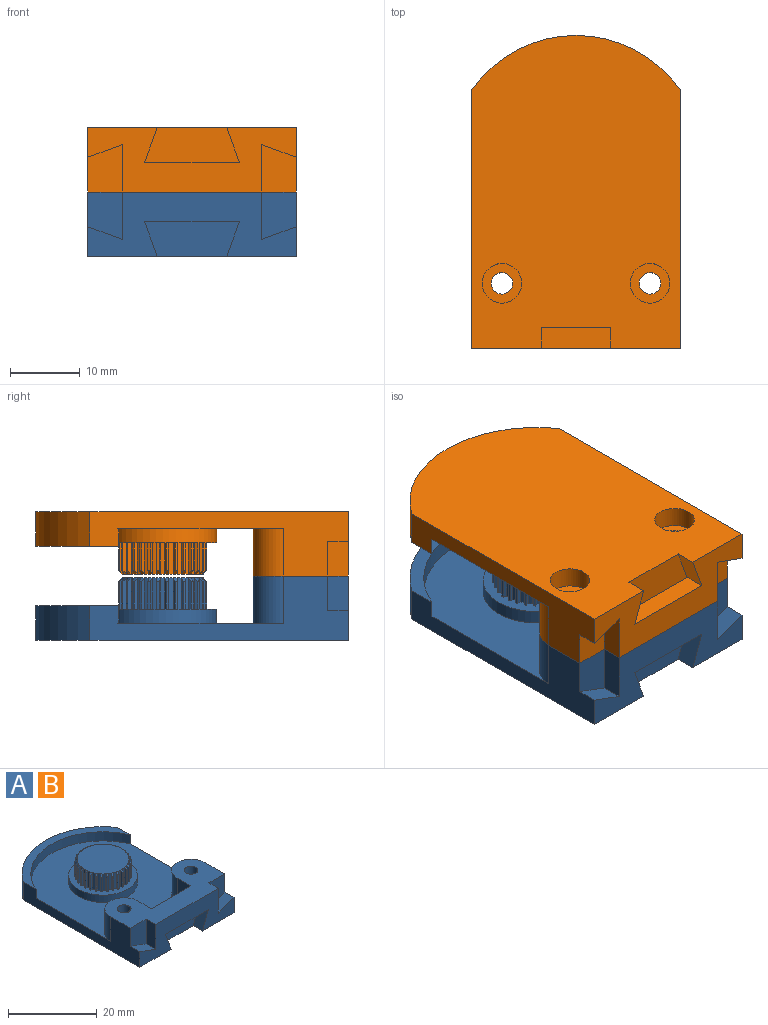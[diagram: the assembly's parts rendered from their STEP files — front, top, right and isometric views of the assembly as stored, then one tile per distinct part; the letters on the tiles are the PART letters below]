
ASSEMBLY  parts=2 mates=1
PART A: 183 faces, bbox 30x45x9.3 mm
  f0: plane 45x30mm, normal (0,0,-1), area 1198.9mm2, adj f3,f4,f5,f162,f163,f165,f176,f178
  f1: plane 12.6x6.77mm, normal (0,1,0), area 85.3mm2, adj f2,f154,f173,f174
  f2: plane 30x13.7mm, normal (0,0,1), area 240mm2, adj f1,f3,f4,f5,f152,f153,f167,f168
  f3: plane 37.17x9.27mm, normal (1,0,0), area 151.5mm2, adj f0,f2,f5,f154,f170,f171,f172,f180
  f4: plane 37.17x9.27mm, normal (-1,0,0), area 151.5mm2, adj f0,f2,f5,f154,f166,f168,f175,f180
  f5: plane 30x9.27mm, normal (0,-1,0), area 159.9mm2, adj f0,f2,f3,f4,f162,f163,f164,f166
  f6: cone r=5.85mm half-angle=45deg, axis (0,0,-1), area 0.3mm2, adj f7,f10,f157,f159
  f7: cylinder r=6.35mm len=4mm, axis (0,0,-1), area 1.3mm2, adj f6,f10,f156,f159
  f8: plane 4.51x0.45mm, normal (0.53,-0.85,0), area 2.2mm2, adj f9,f11,f12,f156
  f9: cylinder r=5.85mm len=4.5mm, axis (0,0,-1), area 2.9mm2, adj f8,f10,f156,f157
  f10: plane 4.51x0.52mm, normal (0.14,0.99,0), area 2.2mm2, adj f6,f7,f9,f156
  f11: cone r=5.85mm half-angle=45deg, axis (0,0,-1), area 0.3mm2, adj f8,f12,f15,f157
  f12: cylinder r=6.35mm len=4mm, axis (0,0,-1), area 1.3mm2, adj f8,f11,f15,f156
  f13: plane 4.51x0.38mm, normal (0.69,-0.72,0), area 2.2mm2, adj f14,f16,f17,f156
  f14: cylinder r=5.85mm len=4.5mm, axis (0,0,-1), area 2.9mm2, adj f13,f15,f156,f157
  f15: plane 4.51x0.53mm, normal (-0.07,1,0), area 2.2mm2, adj f11,f12,f14,f156
  f16: cone r=5.85mm half-angle=45deg, axis (0,0,-1), area 0.3mm2, adj f13,f17,f20,f157
  f17: cylinder r=6.35mm len=4mm, axis (0,0,-1), area 1.3mm2, adj f13,f16,f20,f156
  f18: plane 4.51x0.44mm, normal (0.83,-0.56,0), area 2.2mm2, adj f19,f21,f22,f156
  f19: cylinder r=5.85mm len=4.5mm, axis (0,0,-1), area 2.9mm2, adj f18,f20,f156,f157
  f20: plane 4.51x0.51mm, normal (-0.28,0.96,0), area 2.2mm2, adj f16,f17,f19,f156
  f21: cone r=5.85mm half-angle=45deg, axis (0,0,-1), area 0.3mm2, adj f18,f22,f25,f157
  f22: cylinder r=6.35mm len=4mm, axis (0,0,-1), area 1.3mm2, adj f18,f21,f25,f156
  f23: plane 4.51x0.49mm, normal (0.93,-0.37,0), area 2.2mm2, adj f24,f26,f27,f156
  f24: cylinder r=5.85mm len=4.5mm, axis (0,0,-1), area 2.9mm2, adj f23,f25,f156,f157
  f25: plane 4.51x0.47mm, normal (-0.47,0.88,0), area 2.2mm2, adj f21,f22,f24,f156
  f26: cone r=5.85mm half-angle=45deg, axis (0,0,-1), area 0.3mm2, adj f23,f27,f30,f157
  f27: cylinder r=6.35mm len=4mm, axis (0,0,-1), area 1.3mm2, adj f23,f26,f30,f156
  f28: plane 4.51x0.52mm, normal (0.98,-0.17,0), area 2.2mm2, adj f29,f31,f32,f156
  f29: cylinder r=5.85mm len=4.5mm, axis (0,0,-1), area 2.9mm2, adj f28,f30,f156,f157
  f30: plane 4.51x0.4mm, normal (-0.64,0.77,0), area 2.2mm2, adj f26,f27,f29,f156
  f31: cone r=5.85mm half-angle=45deg, axis (0,0,-1), area 0.3mm2, adj f28,f32,f35,f157
  f32: cylinder r=6.35mm len=4mm, axis (0,0,-1), area 1.3mm2, adj f28,f31,f35,f156
  f33: plane 4.51x0.53mm, normal (1,0.03,0), area 2.2mm2, adj f34,f36,f37,f156
  f34: cylinder r=5.85mm len=4.5mm, axis (0,0,-1), area 2.9mm2, adj f33,f35,f156,f157
  f35: plane 4.51x0.42mm, normal (-0.79,0.62,0), area 2.2mm2, adj f31,f32,f34,f156
  f36: cone r=5.85mm half-angle=45deg, axis (0,0,-1), area 0.3mm2, adj f33,f37,f40,f157
  f37: cylinder r=6.35mm len=4mm, axis (0,0,-1), area 1.3mm2, adj f33,f36,f40,f156
  f38: plane 4.51x0.51mm, normal (0.97,0.24,0), area 2.2mm2, adj f39,f41,f42,f156
  f39: cylinder r=5.85mm len=4.5mm, axis (0,0,-1), area 2.9mm2, adj f38,f40,f156,f157
  f40: plane 4.51x0.47mm, normal (-0.9,0.44,0), area 2.2mm2, adj f36,f37,f39,f156
  f41: cone r=5.85mm half-angle=45deg, axis (0,0,-1), area 0.3mm2, adj f38,f42,f45,f157
  f42: cylinder r=6.35mm len=4mm, axis (0,0,-1), area 1.3mm2, adj f38,f41,f45,f156
  f43: plane 4.51x0.47mm, normal (0.9,0.44,0), area 2.2mm2, adj f44,f46,f47,f156
  f44: cylinder r=5.85mm len=4.5mm, axis (0,0,-1), area 2.9mm2, adj f43,f45,f156,f157
  f45: plane 4.51x0.51mm, normal (-0.97,0.24,0), area 2.2mm2, adj f41,f42,f44,f156
  f46: cone r=5.85mm half-angle=45deg, axis (0,0,-1), area 0.3mm2, adj f43,f47,f50,f157
  f47: cylinder r=6.35mm len=4mm, axis (0,0,-1), area 1.3mm2, adj f43,f46,f50,f156
  f48: plane 4.51x0.42mm, normal (0.79,0.62,0), area 2.2mm2, adj f49,f51,f52,f156
  f49: cylinder r=5.85mm len=4.5mm, axis (0,0,-1), area 2.9mm2, adj f48,f50,f156,f157
  f50: plane 4.51x0.53mm, normal (-1,0.03,0), area 2.2mm2, adj f46,f47,f49,f156
  f51: cone r=5.85mm half-angle=45deg, axis (0,0,-1), area 0.3mm2, adj f48,f52,f55,f157
  f52: cylinder r=6.35mm len=4mm, axis (0,0,-1), area 1.3mm2, adj f48,f51,f55,f156
  f53: plane 4.51x0.4mm, normal (0.64,0.77,0), area 2.2mm2, adj f54,f56,f57,f156
  f54: cylinder r=5.85mm len=4.5mm, axis (0,0,-1), area 2.9mm2, adj f53,f55,f156,f157
  f55: plane 4.51x0.52mm, normal (-0.98,-0.17,0), area 2.2mm2, adj f51,f52,f54,f156
  f56: cone r=5.85mm half-angle=45deg, axis (0,0,-1), area 0.3mm2, adj f53,f57,f60,f157
  f57: cylinder r=6.35mm len=4mm, axis (0,0,-1), area 1.3mm2, adj f53,f56,f60,f156
  f58: plane 4.51x0.47mm, normal (0.47,0.88,0), area 2.2mm2, adj f59,f61,f62,f156
  f59: cylinder r=5.85mm len=4.5mm, axis (0,0,-1), area 2.9mm2, adj f58,f60,f156,f157
  f60: plane 4.51x0.49mm, normal (-0.93,-0.37,0), area 2.2mm2, adj f56,f57,f59,f156
  f61: cone r=5.85mm half-angle=45deg, axis (0,0,-1), area 0.3mm2, adj f58,f62,f65,f157
  f62: cylinder r=6.35mm len=4mm, axis (0,0,-1), area 1.3mm2, adj f58,f61,f65,f156
  f63: plane 4.51x0.51mm, normal (0.28,0.96,0), area 2.2mm2, adj f64,f66,f67,f156
  f64: cylinder r=5.85mm len=4.5mm, axis (0,0,-1), area 2.9mm2, adj f63,f65,f156,f157
  f65: plane 4.51x0.44mm, normal (-0.83,-0.56,0), area 2.2mm2, adj f61,f62,f64,f156
  f66: cone r=5.85mm half-angle=45deg, axis (0,0,-1), area 0.3mm2, adj f63,f67,f70,f157
  f67: cylinder r=6.35mm len=4mm, axis (0,0,-1), area 1.3mm2, adj f63,f66,f70,f156
  f68: plane 4.51x0.53mm, normal (0.07,1,0), area 2.2mm2, adj f69,f71,f72,f156
  f69: cylinder r=5.85mm len=4.5mm, axis (0,0,-1), area 2.9mm2, adj f68,f70,f156,f157
  f70: plane 4.51x0.38mm, normal (-0.69,-0.72,0), area 2.2mm2, adj f66,f67,f69,f156
  f71: cone r=5.85mm half-angle=45deg, axis (0,0,-1), area 0.3mm2, adj f68,f72,f75,f157
  f72: cylinder r=6.35mm len=4mm, axis (0,0,-1), area 1.3mm2, adj f68,f71,f75,f156
  f73: plane 4.51x0.52mm, normal (-0.14,0.99,0), area 2.2mm2, adj f74,f76,f77,f156
  f74: cylinder r=5.85mm len=4.5mm, axis (0,0,-1), area 2.9mm2, adj f73,f75,f156,f157
  f75: plane 4.51x0.45mm, normal (-0.53,-0.85,0), area 2.2mm2, adj f71,f72,f74,f156
  f76: cone r=5.85mm half-angle=45deg, axis (0,0,-1), area 0.3mm2, adj f73,f77,f80,f157
  f77: cylinder r=6.35mm len=4mm, axis (0,0,-1), area 1.3mm2, adj f73,f76,f80,f156
  f78: plane 4.51x0.5mm, normal (-0.34,0.94,0), area 2.2mm2, adj f79,f81,f82,f156
  f79: cylinder r=5.85mm len=4.5mm, axis (0,0,-1), area 2.9mm2, adj f78,f80,f156,f157
  f80: plane 4.51x0.5mm, normal (-0.34,-0.94,0), area 2.2mm2, adj f76,f77,f79,f156
  f81: cone r=5.85mm half-angle=45deg, axis (0,0,-1), area 0.3mm2, adj f78,f82,f85,f157
  f82: cylinder r=6.35mm len=4mm, axis (0,0,-1), area 1.3mm2, adj f78,f81,f85,f156
  f83: plane 4.51x0.45mm, normal (-0.53,0.85,0), area 2.2mm2, adj f84,f86,f87,f156
  f84: cylinder r=5.85mm len=4.5mm, axis (0,0,-1), area 2.9mm2, adj f83,f85,f156,f157
  f85: plane 4.51x0.52mm, normal (-0.14,-0.99,0), area 2.2mm2, adj f81,f82,f84,f156
  f86: cone r=5.85mm half-angle=45deg, axis (0,0,-1), area 0.3mm2, adj f83,f87,f90,f157
  f87: cylinder r=6.35mm len=4mm, axis (0,0,-1), area 1.3mm2, adj f83,f86,f90,f156
  f88: plane 4.51x0.38mm, normal (-0.69,0.72,0), area 2.2mm2, adj f89,f91,f92,f156
  f89: cylinder r=5.85mm len=4.5mm, axis (0,0,-1), area 2.9mm2, adj f88,f90,f156,f157
  f90: plane 4.51x0.53mm, normal (0.07,-1,0), area 2.2mm2, adj f86,f87,f89,f156
  f91: cone r=5.85mm half-angle=45deg, axis (0,0,-1), area 0.3mm2, adj f88,f92,f95,f157
  f92: cylinder r=6.35mm len=4mm, axis (0,0,-1), area 1.3mm2, adj f88,f91,f95,f156
  f93: plane 4.51x0.44mm, normal (-0.83,0.56,0), area 2.2mm2, adj f94,f96,f97,f156
  f94: cylinder r=5.85mm len=4.5mm, axis (0,0,-1), area 2.9mm2, adj f93,f95,f156,f157
  f95: plane 4.51x0.51mm, normal (0.28,-0.96,0), area 2.2mm2, adj f91,f92,f94,f156
  f96: cone r=5.85mm half-angle=45deg, axis (0,0,-1), area 0.3mm2, adj f93,f97,f100,f157
  f97: cylinder r=6.35mm len=4mm, axis (0,0,-1), area 1.3mm2, adj f93,f96,f100,f156
  f98: plane 4.51x0.49mm, normal (-0.93,0.37,0), area 2.2mm2, adj f99,f101,f102,f156
  f99: cylinder r=5.85mm len=4.5mm, axis (0,0,-1), area 2.9mm2, adj f98,f100,f156,f157
  f100: plane 4.51x0.47mm, normal (0.47,-0.88,0), area 2.2mm2, adj f96,f97,f99,f156
  f101: cone r=5.85mm half-angle=45deg, axis (0,0,-1), area 0.3mm2, adj f98,f102,f105,f157
  f102: cylinder r=6.35mm len=4mm, axis (0,0,-1), area 1.3mm2, adj f98,f101,f105,f156
  f103: plane 4.51x0.52mm, normal (-0.98,0.17,0), area 2.2mm2, adj f104,f106,f107,f156
  f104: cylinder r=5.85mm len=4.5mm, axis (0,0,-1), area 2.9mm2, adj f103,f105,f156,f157
  f105: plane 4.51x0.4mm, normal (0.64,-0.77,0), area 2.2mm2, adj f101,f102,f104,f156
  f106: cone r=5.85mm half-angle=45deg, axis (0,0,-1), area 0.3mm2, adj f103,f107,f110,f157
  f107: cylinder r=6.35mm len=4mm, axis (0,0,-1), area 1.3mm2, adj f103,f106,f110,f156
  f108: plane 4.51x0.53mm, normal (-1,-0.03,0), area 2.2mm2, adj f109,f111,f112,f156
  f109: cylinder r=5.85mm len=4.5mm, axis (0,0,-1), area 2.9mm2, adj f108,f110,f156,f157
  f110: plane 4.51x0.42mm, normal (0.79,-0.62,0), area 2.2mm2, adj f106,f107,f109,f156
  f111: cone r=5.85mm half-angle=45deg, axis (0,0,-1), area 0.3mm2, adj f108,f112,f115,f157
  f112: cylinder r=6.35mm len=4mm, axis (0,0,-1), area 1.3mm2, adj f108,f111,f115,f156
  f113: plane 4.51x0.51mm, normal (-0.97,-0.24,0), area 2.2mm2, adj f114,f116,f117,f156
  f114: cylinder r=5.85mm len=4.5mm, axis (0,0,-1), area 2.9mm2, adj f113,f115,f156,f157
  f115: plane 4.51x0.47mm, normal (0.9,-0.44,0), area 2.2mm2, adj f111,f112,f114,f156
  f116: cone r=5.85mm half-angle=45deg, axis (0,0,-1), area 0.3mm2, adj f113,f117,f120,f157
  f117: cylinder r=6.35mm len=4mm, axis (0,0,-1), area 1.3mm2, adj f113,f116,f120,f156
  f118: plane 4.51x0.47mm, normal (-0.9,-0.44,0), area 2.2mm2, adj f119,f121,f122,f156
  f119: cylinder r=5.85mm len=4.5mm, axis (0,0,-1), area 2.9mm2, adj f118,f120,f156,f157
  f120: plane 4.51x0.51mm, normal (0.97,-0.24,0), area 2.2mm2, adj f116,f117,f119,f156
  f121: cone r=5.85mm half-angle=45deg, axis (0,0,-1), area 0.3mm2, adj f118,f122,f125,f157
  f122: cylinder r=6.35mm len=4mm, axis (0,0,-1), area 1.3mm2, adj f118,f121,f125,f156
  f123: plane 4.51x0.42mm, normal (-0.79,-0.62,0), area 2.2mm2, adj f124,f126,f127,f156
  f124: cylinder r=5.85mm len=4.5mm, axis (0,0,-1), area 2.9mm2, adj f123,f125,f156,f157
  f125: plane 4.51x0.53mm, normal (1,-0.03,0), area 2.2mm2, adj f121,f122,f124,f156
  f126: cone r=5.85mm half-angle=45deg, axis (0,0,-1), area 0.3mm2, adj f123,f127,f130,f157
  f127: cylinder r=6.35mm len=4mm, axis (0,0,-1), area 1.3mm2, adj f123,f126,f130,f156
  f128: plane 4.51x0.4mm, normal (-0.64,-0.77,0), area 2.2mm2, adj f129,f131,f132,f156
  f129: cylinder r=5.85mm len=4.5mm, axis (0,0,-1), area 2.9mm2, adj f128,f130,f156,f157
  f130: plane 4.51x0.52mm, normal (0.98,0.17,0), area 2.2mm2, adj f126,f127,f129,f156
  f131: cone r=5.85mm half-angle=45deg, axis (0,0,-1), area 0.3mm2, adj f128,f132,f135,f157
  f132: cylinder r=6.35mm len=4mm, axis (0,0,-1), area 1.3mm2, adj f128,f131,f135,f156
  f133: plane 4.51x0.47mm, normal (-0.47,-0.88,0), area 2.2mm2, adj f134,f136,f137,f156
  f134: cylinder r=5.85mm len=4.5mm, axis (0,0,-1), area 2.9mm2, adj f133,f135,f156,f157
  f135: plane 4.51x0.49mm, normal (0.93,0.37,0), area 2.2mm2, adj f131,f132,f134,f156
  f136: cone r=5.85mm half-angle=45deg, axis (0,0,-1), area 0.3mm2, adj f133,f137,f140,f157
  f137: cylinder r=6.35mm len=4mm, axis (0,0,-1), area 1.3mm2, adj f133,f136,f140,f156
  f138: plane 4.51x0.51mm, normal (-0.28,-0.96,0), area 2.2mm2, adj f139,f141,f142,f156
  f139: cylinder r=5.85mm len=4.5mm, axis (0,0,-1), area 2.9mm2, adj f138,f140,f156,f157
  f140: plane 4.51x0.44mm, normal (0.83,0.56,0), area 2.2mm2, adj f136,f137,f139,f156
  f141: cone r=5.85mm half-angle=45deg, axis (0,0,-1), area 0.3mm2, adj f138,f142,f145,f157
  f142: cylinder r=6.35mm len=4mm, axis (0,0,-1), area 1.3mm2, adj f138,f141,f145,f156
  f143: plane 4.51x0.53mm, normal (-0.07,-1,0), area 2.2mm2, adj f144,f146,f147,f156
  f144: cylinder r=5.85mm len=4.5mm, axis (0,0,-1), area 2.9mm2, adj f143,f145,f156,f157
  f145: plane 4.51x0.38mm, normal (0.69,0.72,0), area 2.2mm2, adj f141,f142,f144,f156
  f146: cone r=5.85mm half-angle=45deg, axis (0,0,-1), area 0.3mm2, adj f143,f147,f150,f157
  f147: cylinder r=6.35mm len=4mm, axis (0,0,-1), area 1.3mm2, adj f143,f146,f150,f156
  f148: plane 4.51x0.52mm, normal (0.14,-0.99,0), area 2.2mm2, adj f149,f151,f156,f158
  f149: cylinder r=5.85mm len=4.5mm, axis (0,0,-1), area 2.9mm2, adj f148,f150,f156,f157
  f150: plane 4.51x0.45mm, normal (0.53,0.85,0), area 2.2mm2, adj f146,f147,f149,f156
  f151: cone r=5.85mm half-angle=45deg, axis (0,0,-1), area 0.3mm2, adj f148,f157,f158,f161
  f152: cylinder r=1.55mm len=6.27mm, axis (0,0,-1), area 61.1mm2, adj f2,f177
  f153: cylinder r=1.55mm len=6.27mm, axis (0,0,-1), area 61.1mm2, adj f2,f179
  f154: plane 38x30mm, normal (0,0,1), area 733.3mm2, adj f1,f3,f4,f155,f172,f173,f174,f175
  f155: cylinder r=7.75mm len=15.5mm, axis (0,0,-1), area 97.4mm2, adj f154,f156
  f156: plane 15.5x15.5mm, normal (0,0,1), area 74.4mm2, adj f7,f8,f9,f10,f12,f13,f14,f15
  f157: plane 11.7x11.7mm, normal (0,0,1), area 107.5mm2, adj f6,f9,f11,f14,f16,f19,f21,f24
  f158: cylinder r=6.35mm len=4mm, axis (0,0,-1), area 1.3mm2, adj f148,f151,f156,f161
  f159: plane 4.51x0.5mm, normal (0.34,-0.94,0), area 2.2mm2, adj f6,f7,f156,f160
  f160: cylinder r=5.85mm len=4.5mm, axis (0,0,-1), area 2.9mm2, adj f156,f157,f159,f161
  f161: plane 4.51x0.5mm, normal (0.34,0.94,0), area 2.2mm2, adj f151,f156,f158,f160
  f162: plane 5x3mm, normal (0.94,0,0.34), area 16mm2, adj f0,f5,f164,f165
  f163: plane 5x3mm, normal (-0.94,0,0.34), area 16mm2, adj f0,f5,f164,f165
  f164: plane 13.64x3mm, normal (0,0,-1), area 40.9mm2, adj f5,f162,f163,f165
  f165: plane 13.64x5mm, normal (0,-1,0), area 59.1mm2, adj f0,f162,f163,f164
  f166: plane 5x3mm, normal (0.34,0,0.94), area 16mm2, adj f4,f5,f167,f168
  f167: plane 6.82x3mm, normal (-1,0,0), area 20.5mm2, adj f2,f5,f166,f168
  f168: plane 6.82x5mm, normal (0,-1,0), area 29.5mm2, adj f2,f4,f166,f167
  f169: plane 6.82x3mm, normal (1,0,0), area 20.5mm2, adj f2,f5,f170,f171
  f170: plane 5x3mm, normal (-0.34,0,0.94), area 16mm2, adj f3,f5,f169,f171
  f171: plane 6.82x5mm, normal (0,-1,0), area 29.5mm2, adj f2,f3,f169,f170
  f172: cylinder r=4.35mm len=8.7mm, axis (0,0,-1), area 92.5mm2, adj f2,f3,f154,f173
  f173: plane 6.77x4.35mm, normal (-1,0,0), area 29.4mm2, adj f1,f2,f154,f172
  f174: plane 6.77x4.35mm, normal (1,0,0), area 29.4mm2, adj f1,f2,f154,f175
  f175: cylinder r=4.35mm len=8.7mm, axis (0,0,-1), area 92.5mm2, adj f2,f4,f154,f174
  f176: cylinder r=2.85mm len=5.7mm, axis (0,0,-1), area 53.7mm2, adj f0,f177
  f177: plane 5.7x5.7mm, normal (0,0,-1), area 18mm2, adj f152,f176
  f178: cylinder r=2.85mm len=5.7mm, axis (0,0,-1), area 53.7mm2, adj f0,f179
  f179: plane 5.7x5.7mm, normal (0,0,-1), area 18mm2, adj f153,f178
  f180: cylinder r=16.29mm len=30mm, axis (0,0,-1), area 95.3mm2, adj f3,f4,f154,f182
  f181: cylinder r=18.29mm len=30mm, axis (0,0,-1), area 175.9mm2, adj f0,f3,f4,f182
  f182: plane 30x11.94mm, normal (0,0,1), area 72.9mm2, adj f3,f4,f180,f181
PART B: same geometry as A
PLACE A t=(-10.11,2.59,1.52)mm
PLACE B rot(axis=(0,1,0),180deg) t=(-10.11,2.59,20.06)mm
MATE fastened B.f2 <-> A.f2  axis (0,0,-1) through (-10.11,-24.12,10.79)mm
